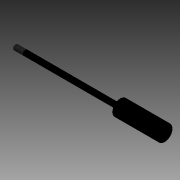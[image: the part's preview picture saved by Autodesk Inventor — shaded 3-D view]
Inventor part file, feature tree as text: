
AUTODESK INVENTOR PART (.ipt)
format: ipt  version: 2014 SP2 (Build 180246200, 246)  size: 138,240 bytes
history: native  units: in
note: dims shown in document units (in); Inventor stores cm internally (conversion verified against a paired STEP export)
features: other x91, revolve x3, sketch x3, thread x1
ambient origin geometry x8: Origin, YZ Plane, XZ Plane, XY Plane, X Axis, Y Axis, Z Axis, Center Point
bodies: Solid1 (feature_tree)
feature tree (98):
  revolve  "Revolution1"  Angle=360.0deg
  revolve  "Revolution2"  Angle=360.0deg
  thread  "Thread1"  [1 undecoded]
  revolve  "Revolution3"  [1 undecoded]
  other  "dia1_XY"
  other  "dia1_YZ"
  other  "dia1_ZX"
  other  "dia1_X"
  other  "dia1_Y"
  other  "dia1_Z"
  other  "dia1_Center"
  other  "dia12_XY"
  other  "dia12_YZ"
  other  "dia12_ZX"
  other  "dia12_X"
  other  "dia12_Y"
  other  "dia12_Z"
  other  "dia12_Center"
  other  "dia1r_XY"
  other  "dia1r_YZ"
  other  "dia1r_ZX"
  other  "dia1r_X"
  other  "dia1r_Y"
  other  "dia1r_Z"
  other  "dia1r_Center"
  other  "dia2_XY"
  other  "dia2_YZ"
  other  "dia2_ZX"
  other  "dia2_X"
  other  "dia2_Y"
  other  "dia2_Z"
  other  "dia2_Center"
  other  "dia22_XY"
  other  "dia22_YZ"
  other  "dia22_ZX"
  other  "dia22_X"
  other  "dia22_Y"
  other  "dia22_Z"
  other  "dia22_Center"
  other  "dia2r_XY"
  other  "dia2r_YZ"
  other  "dia2r_ZX"
  other  "dia2r_X"
  other  "dia2r_Y"
  other  "dia2r_Z"
  other  "dia2r_Center"
  other  "rl1_XY"
  other  "rl1_YZ"
  other  "rl1_ZX"
  other  "rl1_X"
  other  "rl1_Y"
  other  "rl1_Z"
  other  "rl1_Center"
  other  "rl2_XY"
  other  "rl2_YZ"
  other  "rl2_ZX"
  other  "rl2_X"
  other  "rl2_Y"
  other  "rl2_Z"
  other  "rl2_Center"
  other  "rod_cp_XY"
  other  "rod_cp_YZ"
  other  "rod_cp_ZX"
  other  "rod_cp_X"
  other  "rod_cp_Y"
  other  "rod_cp_Z"
  other  "rod_cp_Center"
  other  "stroke1_XY"
  other  "stroke1_YZ"
  other  "stroke1_ZX"
  other  "stroke1_X"
  other  "stroke1_Y"
  other  "stroke1_Z"
  other  "stroke1_Center"
  other  "thd1_XY"
  other  "thd1_YZ"
  other  "thd1_ZX"
  other  "thd1_X"
  other  "thd1_Y"
  other  "thd1_Z"
  other  "thd1_Center"
  other  "thd2_XY"
  other  "thd2_YZ"
  other  "thd2_ZX"
  other  "thd2_X"
  other  "thd2_Y"
  other  "thd2_Z"
  other  "thd2_Center"
  other  "to_rod_clevis_XY"
  other  "to_rod_clevis_YZ"
  other  "to_rod_clevis_ZX"
  other  "to_rod_clevis_X"
  other  "to_rod_clevis_Y"
  other  "to_rod_clevis_Z"
  other  "to_rod_clevis_Center"
  sketch  "Sketch_1"  dims[d0=360.0deg d1=360.0deg]
  sketch  "Sketch_3"  dims[d2=0.4787in d3=0.0in d4=360.0deg]
  sketch  "Sketch_30"  dims[d5=0.0in d6=0.0in d7=0.0in d8=0.0in d9=0.0in d10=0.0in]
note: 2 required parameter values undecoded (feature->parameter linkage not recoverable at this tier; creation-order binding heuristic only, values carry confidence <= 0.55)
